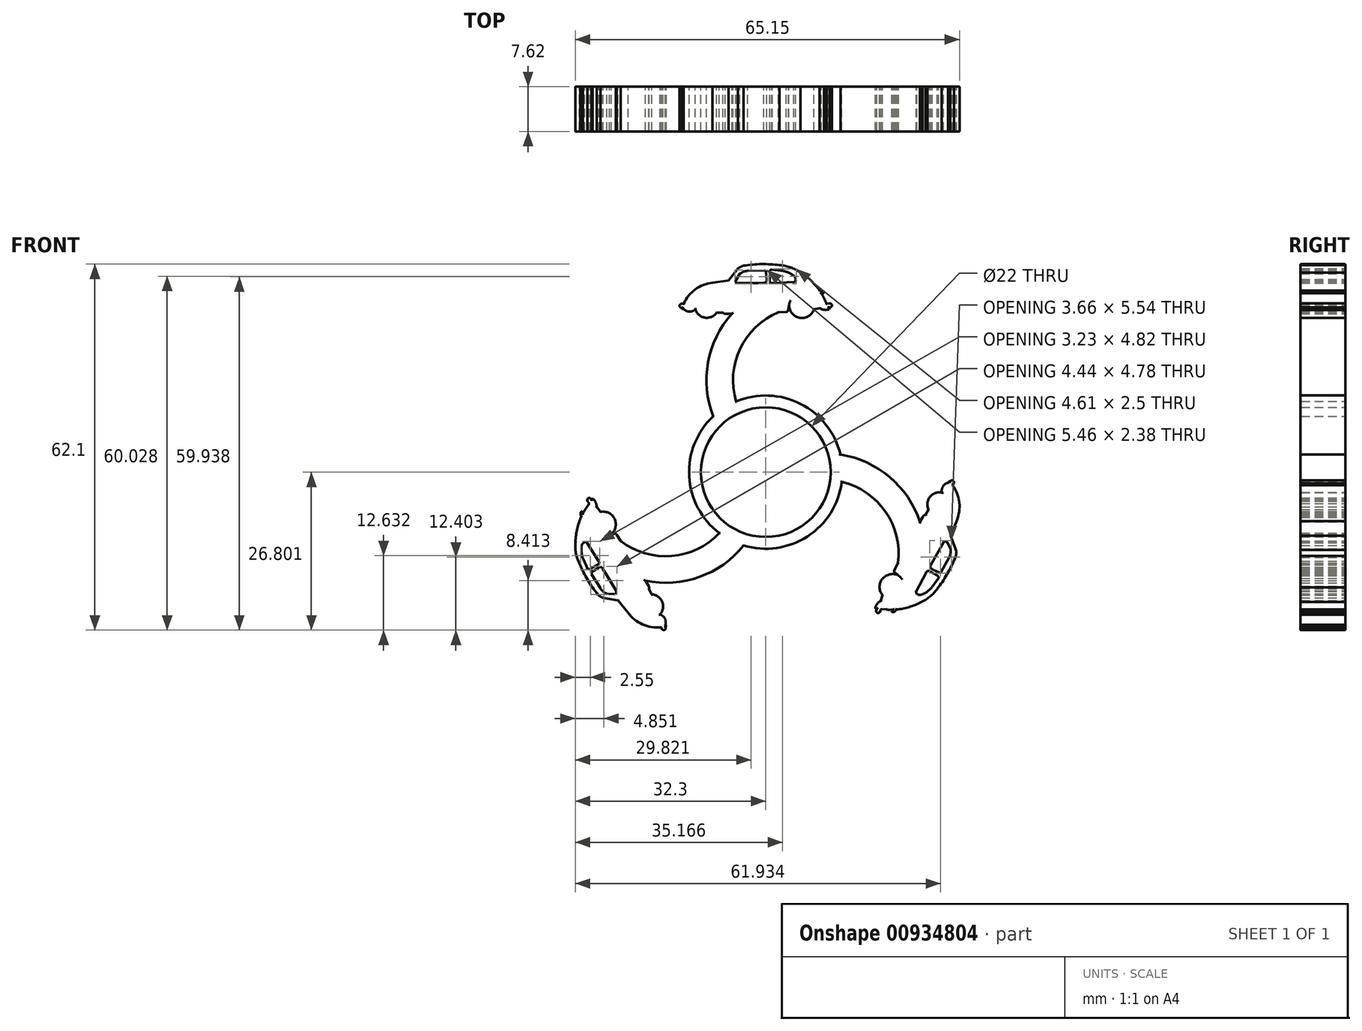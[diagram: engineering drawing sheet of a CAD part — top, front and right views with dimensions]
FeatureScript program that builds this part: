
annotation { "Feature Type Name" : "Feature", "Feature Type Description" : "" }
export const myFeature = defineFeature(function(context is Context, id is Id, definition is map)
    precondition{}
    {
        {
            var Q0;
            Q0=qCreatedBy(makeId("Front.planeOp"),FACE);
            var sketch = newSketch(context, id + "F0", { "sketchPlane" : qUnion([Q0])});
            skArc(sketch, "E0", {"start": v(-9, 14.46) * mm, "mid": v(-11.94, 13.3) * mm, "end": v(-13.92, 10.85) * mm});
            skArc(sketch, "E1", {"start": v(5.88, 16.16) * mm, "mid": v(4.19, 17.04) * mm, "end": v(2.31, 17.41) * mm});
            skArc(sketch, "E2", {"start": v(-11.95, 9.91) * mm, "mid": v(-10.3, 8.52) * mm, "end": v(-8.3, 9.38) * mm});
            skArc(sketch, "E3", {"start": v(3.95, 10.62) * mm, "mid": v(5.76, 8.48) * mm, "end": v(8.18, 9.91) * mm});
            skPoint(sketch, "E4.first.point", {"position": v(-7.38, 9.64) * mm});
            skPoint(sketch, "E4.second.point", {"position": v(-12.35, 9.96) * mm});
            skPoint(sketch, "E4.third.point", {"position": v(-12.18, 8.98) * mm});
            skPoint(sketch, "E5.first.point", {"position": v(4.32, 11.24) * mm});
            skPoint(sketch, "E5.second.point", {"position": v(8.47, 9.2) * mm});
            skPoint(sketch, "E5.third.point", {"position": v(6.12, 12.43) * mm});
            skLineSegment(sketch, "E6", {"start": v(-6.33, 14.84) * mm, "end": v(-4.7, 16.85) * mm});
            skLineSegment(sketch, "E7", {"start": v(-6.33, 14.84) * mm, "end": v(-9, 14.46) * mm});
            skPoint(sketch, "E8.second.point", {"position": v(-1.28, 12.75) * mm});
            skPoint(sketch, "E8.third.point", {"position": v(-0.45, 14.03) * mm});
            skPoint(sketch, "E9.first.point", {"position": v(8.75, 10.46) * mm});
            skPoint(sketch, "E9.second.point", {"position": v(10.03, 11.1) * mm});
            skPoint(sketch, "E9.third.point", {"position": v(9.87, 11.34) * mm});
            skPoint(sketch, "E10.first.point", {"position": v(8.43, 11.1) * mm});
            skPoint(sketch, "E10.second.point", {"position": v(11.08, 13.13) * mm});
            skPoint(sketch, "E10.third.point", {"position": v(10.99, 13.19) * mm});
            skPoint(sketch, "E11.first.point", {"position": v(7.66, 14.8) * mm});
            skPoint(sketch, "E11.second.point", {"position": v(-6.04, -1.6) * mm});
            skPoint(sketch, "E11.third.point", {"position": v(8.43, 0) * mm});
            skArc(sketch, "E12", {"start": v(-14.24, 10) * mm, "mid": v(-14.07, 9.98) * mm, "end": v(-13.9, 9.97) * mm});
            skPoint(sketch, "E12.first.point", {"position": v(-12.18, 10.81) * mm});
            skPoint(sketch, "E12.second.point", {"position": v(-15.7, 13.16) * mm});
            skPoint(sketch, "E12.third.point", {"position": v(-15.23, 10.47) * mm});
            skArc(sketch, "E13", {"start": v(-7.27, 9.38) * mm, "mid": v(-6.98, 9.18) * mm, "end": v(-6.64, 9.16) * mm});
            skPoint(sketch, "E13.second.point", {"position": v(-6.18, 9.92) * mm});
            skPoint(sketch, "E13.third.point", {"position": v(-6.88, 9.15) * mm});
            skLineSegment(sketch, "E14.trimOffspring", {"start": v(-6.88, 9.15) * mm, "end": v(-6.64, 9.16) * mm});
            skArc(sketch, "E15.trimOffspring", {"start": v(-3.79, 17.33) * mm, "mid": v(-4.26, 17.13) * mm, "end": v(-4.7, 16.85) * mm});
            skArc(sketch, "E16.trimOffspring", {"start": v(11.08, 13.13) * mm, "mid": v(11.04, 13.16) * mm, "end": v(10.99, 13.19) * mm});
            skArc(sketch, "E17.trimOffspring", {"start": v(9.96, 11.68) * mm, "mid": v(9.71, 12.17) * mm, "end": v(9.43, 12.65) * mm});
            skPoint(sketch, "E18.first.point", {"position": v(-7.48, 10.06) * mm});
            skPoint(sketch, "E18.second.point", {"position": v(-12.85, 9.43) * mm});
            skPoint(sketch, "E18.third.point", {"position": v(-11.36, 7.32) * mm});
            skArc(sketch, "E19", {"start": v(2.31, 17.41) * mm, "mid": v(-0.74, 17.6) * mm, "end": v(-3.79, 17.33) * mm});
            skPoint(sketch, "E19.second.point", {"position": v(2.31, -24.55) * mm});
            skPoint(sketch, "E20.end.orphan", {"position": v(2.31, 17.41) * mm});
            skArc(sketch, "E21", {"start": v(9.86, 12.65) * mm, "mid": v(9.6, 13.04) * mm, "end": v(9.13, 13.1) * mm});
            skPoint(sketch, "E21.first.point", {"position": v(9.13, 13.1) * mm});
            skPoint(sketch, "E21.second.point", {"position": v(9.36, 12) * mm});
            skPoint(sketch, "E21.third.point", {"position": v(9.7, 12.18) * mm});
            skLineSegment(sketch, "E22", {"start": v(9.86, 12.65) * mm, "end": v(9.43, 12.65) * mm});
            skArc(sketch, "E23.trimOffspring", {"start": v(9.13, 13.1) * mm, "mid": v(7.67, 14.8) * mm, "end": v(5.88, 16.16) * mm});
            skLineSegment(sketch, "E24", {"start": v(9.96, 11.68) * mm, "end": v(10.35, 10.9) * mm});
            skArc(sketch, "E25", {"start": v(10.9, 10.25) * mm, "mid": v(11.21, 10.61) * mm, "end": v(10.85, 10.93) * mm});
            skLineSegment(sketch, "E26", {"start": v(10.9, 10.25) * mm, "end": v(10.67, 10.23) * mm});
            skLineSegment(sketch, "E27", {"start": v(10.85, 10.93) * mm, "end": v(10.35, 10.9) * mm});
            skPoint(sketch, "E27.endSnap0", {"position": v(10.38, 10.82) * mm});
            skPoint(sketch, "E28.orphan", {"position": v(10.38, 10.9) * mm});
            skArc(sketch, "E29", {"start": v(-14.25, 10.85) * mm, "mid": v(-14.6, 10.54) * mm, "end": v(-14.3, 10.18) * mm});
            skArc(sketch, "E30.trimOffspring", {"start": v(-14.18, 10.18) * mm, "mid": v(-14.2, 10.1) * mm, "end": v(-14.24, 10) * mm});
            skLineSegment(sketch, "E31", {"start": v(-14.29, 10.85) * mm, "end": v(-13.92, 10.85) * mm});
            skLineSegment(sketch, "E32", {"start": v(-14.3, 10.18) * mm, "end": v(-14.18, 10.18) * mm});
            skPoint(sketch, "E33.orphan", {"position": v(-13.91, 10.19) * mm});
            skPoint(sketch, "E34.orphan", {"position": v(-14.18, 10.19) * mm});
            skLineSegment(sketch, "E35.trimOffspring", {"start": v(10.67, 10.23) * mm, "end": v(10.8, 9.96) * mm});
            skPoint(sketch, "E36.first.point", {"position": v(4.65, 11.8) * mm});
            skPoint(sketch, "E36.second.point", {"position": v(7.99, 8.17) * mm});
            skPoint(sketch, "E36.third.point", {"position": v(8.67, 9.2) * mm});
            skArc(sketch, "E37", {"start": v(3.48, 9.5) * mm, "mid": v(3.69, 9.57) * mm, "end": v(3.8, 9.77) * mm});
            skPoint(sketch, "E37.first.point", {"position": v(3.8, 9.85) * mm});
            skPoint(sketch, "E37.second.point", {"position": v(3.15, 9.78) * mm});
            skPoint(sketch, "E37.third.point", {"position": v(3.48, 9.5) * mm});
            skLineSegment(sketch, "E38", {"start": v(3.88, 10.28) * mm, "end": v(3.8, 9.77) * mm});
            skArc(sketch, "E39.trimOffspring", {"start": v(3.95, 10.62) * mm, "mid": v(3.9, 10.45) * mm, "end": v(3.88, 10.28) * mm});
            skPoint(sketch, "E40.first.point", {"position": v(-0.4, 16.47) * mm});
            skPoint(sketch, "E40.second.point", {"position": v(-0.1, 15.95) * mm});
            skPoint(sketch, "E40.third.point", {"position": v(-0.25, 15.93) * mm});
            skArc(sketch, "E41", {"start": v(-0.35, 14.4) * mm, "mid": v(0.04, 14.58) * mm, "end": v(0.14, 15) * mm});
            skPoint(sketch, "E41.first.point", {"position": v(0.14, 14.78) * mm});
            skPoint(sketch, "E41.second.point", {"position": v(-0.81, 15.05) * mm});
            skPoint(sketch, "E41.third.point", {"position": v(-0.35, 14.4) * mm});
            skArc(sketch, "E42", {"start": v(-5.03, 14.94) * mm, "mid": v(-5.07, 14.55) * mm, "end": v(-4.73, 14.35) * mm});
            skPoint(sketch, "E42.first.point", {"position": v(-4.93, 14.4) * mm});
            skPoint(sketch, "E42.second.point", {"position": v(-4.52, 15) * mm});
            skPoint(sketch, "E42.third.point", {"position": v(-4.7, 15.07) * mm});
            skArc(sketch, "E43", {"start": v(-3.04, 16.45) * mm, "mid": v(-3.75, 16.32) * mm, "end": v(-4.37, 15.95) * mm});
            skPoint(sketch, "E43.first.point", {"position": v(-4.37, 15.95) * mm});
            skPoint(sketch, "E43.second.point", {"position": v(-1.65, 12.8) * mm});
            skPoint(sketch, "E43.third.point", {"position": v(-0.98, 14.72) * mm});
            skLineSegment(sketch, "E44", {"start": v(-4.37, 15.95) * mm, "end": v(-5.05, 14.9) * mm});
            skLineSegment(sketch, "E45", {"start": v(-3.04, 16.45) * mm, "end": v(-0.23, 16.53) * mm});
            skLineSegment(sketch, "E46", {"start": v(-4.73, 14.35) * mm, "end": v(-0.35, 14.4) * mm});
            skLineSegment(sketch, "E47", {"start": v(0.14, 15) * mm, "end": v(0.07, 16.24) * mm});
            skArc(sketch, "E48.trimOffspring", {"start": v(0.07, 16.24) * mm, "mid": v(-0.1, 16.5) * mm, "end": v(-0.4, 16.47) * mm});
            skArc(sketch, "E49.trimOffspring", {"start": v(-5.03, 14.95) * mm, "mid": v(-5.03, 14.95) * mm, "end": v(-5.03, 14.94) * mm});
            skArc(sketch, "E50", {"start": v(1, 16.68) * mm, "mid": v(0.74, 16.54) * mm, "end": v(0.66, 16.26) * mm});
            skPoint(sketch, "E50.first.point", {"position": v(0.66, 16.33) * mm});
            skPoint(sketch, "E50.second.point", {"position": v(1.43, 16.2) * mm});
            skPoint(sketch, "E50.third.point", {"position": v(0.85, 15.96) * mm});
            skArc(sketch, "E51", {"start": v(0.67, 14.75) * mm, "mid": v(0.79, 14.45) * mm, "end": v(1.11, 14.4) * mm});
            skPoint(sketch, "E51.first.point", {"position": v(0.67, 14.75) * mm});
            skPoint(sketch, "E51.second.point", {"position": v(1.33, 14.68) * mm});
            skPoint(sketch, "E51.third.point", {"position": v(1.32, 14.78) * mm});
            skPoint(sketch, "E52.first.point", {"position": v(5, 14.62) * mm});
            skPoint(sketch, "E52.second.point", {"position": v(3.45, 15.3) * mm});
            skPoint(sketch, "E52.third.point", {"position": v(3.55, 14.43) * mm});
            skArc(sketch, "E53", {"start": v(0.66, 16.29) * mm, "mid": v(0.66, 16.29) * mm, "end": v(0.66, 16.29) * mm});
            skPoint(sketch, "E53.first.point", {"position": v(4.74, 15.63) * mm});
            skPoint(sketch, "E53.second.point", {"position": v(-0.68, 8.76) * mm});
            skPoint(sketch, "E53.third.point", {"position": v(1.58, 16.5) * mm});
            skArc(sketch, "E54", {"start": v(4.77, 14.54) * mm, "mid": v(4.95, 14.63) * mm, "end": v(5.06, 14.8) * mm});
            skPoint(sketch, "E54.first.point", {"position": v(4.77, 14.54) * mm});
            skPoint(sketch, "E54.second.point", {"position": v(4.56, 15.33) * mm});
            skPoint(sketch, "E54.third.point", {"position": v(4.52, 15.32) * mm});
            skLineSegment(sketch, "E55", {"start": v(1.11, 14.4) * mm, "end": v(4.77, 14.54) * mm});
            skLineSegment(sketch, "E56", {"start": v(1, 16.68) * mm, "end": v(2.59, 16.5) * mm});
            skLineSegment(sketch, "E57", {"start": v(0.66, 16.33) * mm, "end": v(0.67, 14.75) * mm});
            skArc(sketch, "E58.trimOffspring", {"start": v(5.06, 14.8) * mm, "mid": v(5.02, 15.26) * mm, "end": v(4.74, 15.63) * mm});
            skArc(sketch, "E59.trimOffspring", {"start": v(4.74, 15.63) * mm, "mid": v(3.72, 16.2) * mm, "end": v(2.59, 16.5) * mm});
            skPoint(sketch, "E60.first.point", {"position": v(-13.14, 9.56) * mm});
            skPoint(sketch, "E60.second.point", {"position": v(-12.49, 12.22) * mm});
            skPoint(sketch, "E60.third.point", {"position": v(-12.69, 12.26) * mm});
            skArc(sketch, "E61.trimOffspring", {"start": v(-13.9, 9.97) * mm, "mid": v(-12.93, 9.54) * mm, "end": v(-11.95, 9.91) * mm});
            skLineSegment(sketch, "E62", {"start": v(-8.3, 9.38) * mm, "end": v(-7.27, 9.38) * mm});
            skLineSegment(sketch, "E63", {"start": v(8.18, 9.91) * mm, "end": v(9.21, 10.1) * mm});
            skArc(sketch, "E64.trimOffspring", {"start": v(9.21, 10.1) * mm, "mid": v(10, 9.84) * mm, "end": v(10.8, 9.96) * mm});
            skPoint(sketch, "E65.1.0", {"position": v(-30.88, -30.27) * mm});
            skPoint(sketch, "E65.1.1", {"position": v(-19.6, -43.67) * mm});
            skPoint(sketch, "E65.1.2", {"position": v(-16.78, -44.97) * mm});
            skPoint(sketch, "E65.1.3", {"position": v(-31.57, -33.25) * mm});
            skPoint(sketch, "E65.1.4", {"position": v(-27.95, -34.77) * mm});
            skPoint(sketch, "E65.1.5", {"position": v(-30.08, -23.67) * mm});
            skPoint(sketch, "E65.1.6", {"position": v(-32.24, -23.63) * mm});
            skPoint(sketch, "E65.1.7", {"position": v(-31.98, -27.31) * mm});
            skPoint(sketch, "E65.1.8", {"position": v(-29.8, -34.14) * mm});
            skPoint(sketch, "E65.1.9", {"position": v(-17.04, -42.7) * mm});
            skPoint(sketch, "E65.1.10", {"position": v(-25.76, -28.18) * mm});
            skPoint(sketch, "E65.1.11", {"position": v(-10.93, -30.98) * mm});
            skPoint(sketch, "E65.1.12", {"position": v(4.78, -12.27) * mm});
            skPoint(sketch, "E65.1.13", {"position": v(-29.6, -30.69) * mm});
            skPoint(sketch, "E65.1.14", {"position": v(-22.57, -31.51) * mm});
            skPoint(sketch, "E65.1.15", {"position": v(-32.24, -23.51) * mm});
            skPoint(sketch, "E65.1.16", {"position": v(-19.99, -37.76) * mm});
            skPoint(sketch, "E65.1.17", {"position": v(-29.57, -33.8) * mm});
            skPoint(sketch, "E65.1.18", {"position": v(-29.4, -35.13) * mm});
            skPoint(sketch, "E65.1.19", {"position": v(-17.06, -43.92) * mm});
            skPoint(sketch, "E65.1.20", {"position": v(-19.81, -37.08) * mm});
            skPoint(sketch, "E65.1.21", {"position": v(-17.01, -41.58) * mm});
            skPoint(sketch, "E65.1.22", {"position": v(-30.3, -31.21) * mm});
            skPoint(sketch, "E65.1.23", {"position": v(-25.28, -28.28) * mm});
            skPoint(sketch, "E65.1.24", {"position": v(-26.96, -38.31) * mm});
            skPoint(sketch, "E65.1.25", {"position": v(-26.03, -38.15) * mm});
            skPoint(sketch, "E65.1.26", {"position": v(-25.73, -34.03) * mm});
            skPoint(sketch, "E65.1.27", {"position": v(-27.63, -23.64) * mm});
            skPoint(sketch, "E65.1.28", {"position": v(-20.3, -38.05) * mm});
            skPoint(sketch, "E65.1.29", {"position": v(-17.07, -42.39) * mm});
            skPoint(sketch, "E65.1.30", {"position": v(-27.25, -33.95) * mm});
            skPoint(sketch, "E65.1.31", {"position": v(-17.78, -42.23) * mm});
            skPoint(sketch, "E65.1.32", {"position": v(-19.54, -19.25) * mm});
            skPoint(sketch, "E65.1.33", {"position": v(-15.99, -40.05) * mm});
            skPoint(sketch, "E65.1.34", {"position": v(-20.83, -36.87) * mm});
            skPoint(sketch, "E65.1.35", {"position": v(-28.2, -33.82) * mm});
            skPoint(sketch, "E65.1.36", {"position": v(-18.87, -46.72) * mm});
            skPoint(sketch, "E65.1.37", {"position": v(-26.4, -23.72) * mm});
            skPoint(sketch, "E65.1.38", {"position": v(-30.5, -29.52) * mm});
            skPoint(sketch, "E65.1.39", {"position": v(-29.15, -27.46) * mm});
            skLineSegment(sketch, "E65.1.40", {"start": v(-19.81, -37.08) * mm, "end": v(-20.4, -36.13) * mm});
            skPoint(sketch, "E65.1.41", {"position": v(-31.24, -25.19) * mm});
            skPoint(sketch, "E65.1.42", {"position": v(-29.96, -23.41) * mm});
            skArc(sketch, "E65.1.43", {"start": v(-17.94, -41.85) * mm, "mid": v(-17.56, -39.72) * mm, "end": v(-19.3, -38.43) * mm});
            skPoint(sketch, "E65.1.44", {"position": v(-27.53, -23.81) * mm});
            skPoint(sketch, "E65.1.45", {"position": v(-29.9, -22.97) * mm});
            skPoint(sketch, "E65.1.46", {"position": v(-30.72, -24.23) * mm});
            skPoint(sketch, "E65.1.47", {"position": v(-18.6, -42.5) * mm});
            skPoint(sketch, "E65.1.48", {"position": v(-30.86, -30.29) * mm});
            skPoint(sketch, "E65.1.49", {"position": v(-26.05, -37.96) * mm});
            skPoint(sketch, "E65.1.50", {"position": v(-27.62, -34.05) * mm});
            skPoint(sketch, "E65.1.51", {"position": v(-19.67, -43.47) * mm});
            skPoint(sketch, "E65.1.52", {"position": v(-17.2, -43.69) * mm});
            skPoint(sketch, "E65.1.53", {"position": v(-29, -34.73) * mm});
            skPoint(sketch, "E65.1.54", {"position": v(-27.88, -28.42) * mm});
            skPoint(sketch, "E65.1.55", {"position": v(-30.4, -33.42) * mm});
            skPoint(sketch, "E65.1.56", {"position": v(-25.6, -34.38) * mm});
            skPoint(sketch, "E65.1.57", {"position": v(-27.22, -28.43) * mm});
            skPoint(sketch, "E65.1.58", {"position": v(-28.76, -24.2) * mm});
            skPoint(sketch, "E65.1.59", {"position": v(-25.37, -28.7) * mm});
            skPoint(sketch, "E65.1.60", {"position": v(-28.79, -32.8) * mm});
            skPoint(sketch, "E65.1.61", {"position": v(-25.33, -38.02) * mm});
            skPoint(sketch, "E65.1.62", {"position": v(-30.3, -29.68) * mm});
            skPoint(sketch, "E65.1.63", {"position": v(-27.59, -34.76) * mm});
            skPoint(sketch, "E65.1.64", {"position": v(-29.15, -24.8) * mm});
            skArc(sketch, "E65.1.65", {"start": v(-23.35, -41.58) * mm, "mid": v(-20.88, -43.53) * mm, "end": v(-17.77, -44.03) * mm});
            skPoint(sketch, "E65.1.66", {"position": v(-29.1, -34.62) * mm});
            skArc(sketch, "E65.1.67", {"start": v(-26.5, -28.44) * mm, "mid": v(-25.56, -25.8) * mm, "end": v(-28, -24.42) * mm});
            skPoint(sketch, "E65.1.68", {"position": v(-30.4, -24.44) * mm});
            skPoint(sketch, "E65.1.69", {"position": v(-28.7, -32.74) * mm});
            skArc(sketch, "E65.1.70", {"start": v(-31.24, -25.19) * mm, "mid": v(-31.98, -27.3) * mm, "end": v(-32.26, -29.53) * mm});
            skPoint(sketch, "E65.1.71", {"position": v(-28.44, -33.35) * mm});
            skPoint(sketch, "E65.1.72", {"position": v(-31.23, -30.26) * mm});
            skPoint(sketch, "E65.1.73", {"position": v(-30.08, -33.41) * mm});
            skPoint(sketch, "E65.1.74", {"position": v(-29.96, -23) * mm});
            skLineSegment(sketch, "E65.1.75", {"start": v(-25.01, -39.45) * mm, "end": v(-23.35, -41.58) * mm});
            skArc(sketch, "E65.1.76", {"start": v(-19.82, -37.53) * mm, "mid": v(-19.78, -37.18) * mm, "end": v(-19.94, -36.87) * mm});
            skLineSegment(sketch, "E65.1.77", {"start": v(-19.3, -38.43) * mm, "end": v(-19.82, -37.53) * mm});
            skArc(sketch, "E65.1.78", {"start": v(-28.44, -38.5) * mm, "mid": v(-28.03, -38.8) * mm, "end": v(-27.57, -39.04) * mm});
            skArc(sketch, "E65.1.79", {"start": v(-32.26, -29.53) * mm, "mid": v(-32.18, -31.44) * mm, "end": v(-31.57, -33.25) * mm});
            skArc(sketch, "E65.1.80", {"start": v(-31.57, -33.25) * mm, "mid": v(-30.2, -35.99) * mm, "end": v(-28.44, -38.5) * mm});
            skLineSegment(sketch, "E65.1.81", {"start": v(-25.01, -39.45) * mm, "end": v(-27.57, -39.04) * mm});
            skArc(sketch, "E65.1.82", {"start": v(-17.02, -43.57) * mm, "mid": v(-17.12, -42.52) * mm, "end": v(-17.94, -41.85) * mm});
            skLineSegment(sketch, "E65.1.84", {"start": v(-28.05, -37.4) * mm, "end": v(-29.52, -35.01) * mm});
            skLineSegment(sketch, "E65.1.85", {"start": v(-26.17, -28.32) * mm, "end": v(-25.69, -28.14) * mm});
            skArc(sketch, "E65.1.86", {"start": v(-28.05, -37.4) * mm, "mid": v(-27.58, -37.95) * mm, "end": v(-26.96, -38.31) * mm});
            skLineSegment(sketch, "E65.1.87", {"start": v(-28.35, -32.78) * mm, "end": v(-30.3, -29.68) * mm});
            skArc(sketch, "E65.1.88", {"start": v(-31.23, -30.26) * mm, "mid": v(-31.22, -31.43) * mm, "end": v(-30.9, -32.56) * mm});
            skLineSegment(sketch, "E65.1.89", {"start": v(-25.39, -37.82) * mm, "end": v(-27.62, -34.05) * mm});
            skArc(sketch, "E65.1.90", {"start": v(-26.5, -28.44) * mm, "mid": v(-26.33, -28.39) * mm, "end": v(-26.17, -28.32) * mm});
            skArc(sketch, "E65.1.91", {"start": v(-30.3, -29.68) * mm, "mid": v(-30.47, -29.58) * mm, "end": v(-30.68, -29.57) * mm});
            skArc(sketch, "E65.1.92", {"start": v(-25.28, -28.28) * mm, "mid": v(-25.46, -28.14) * mm, "end": v(-25.69, -28.14) * mm});
            skArc(sketch, "E65.1.93", {"start": v(-30.68, -29.57) * mm, "mid": v(-31.05, -29.83) * mm, "end": v(-31.23, -30.26) * mm});
            skLineSegment(sketch, "E65.1.94", {"start": v(-28, -24.42) * mm, "end": v(-28.67, -23.62) * mm});
            skArc(sketch, "E65.1.95", {"start": v(-31.2, -24.33) * mm, "mid": v(-31.42, -24.75) * mm, "end": v(-31.24, -25.19) * mm});
            skLineSegment(sketch, "E65.1.96", {"start": v(-30.27, -34.03) * mm, "end": v(-30.9, -32.56) * mm});
            skArc(sketch, "E65.1.97", {"start": v(-30.42, -23.76) * mm, "mid": v(-30.72, -24.22) * mm, "end": v(-31, -24.7) * mm});
            skArc(sketch, "E65.1.98", {"start": v(-32.24, -23.51) * mm, "mid": v(-32.24, -23.57) * mm, "end": v(-32.24, -23.63) * mm});
            skArc(sketch, "E65.1.99", {"start": v(-28.44, -33.35) * mm, "mid": v(-28.23, -33.1) * mm, "end": v(-28.35, -32.78) * mm});
            skArc(sketch, "E65.1.100", {"start": v(-29.43, -34.6) * mm, "mid": v(-29.57, -34.88) * mm, "end": v(-29.4, -35.13) * mm});
            skLineSegment(sketch, "E65.1.101", {"start": v(-28.4, -33.93) * mm, "end": v(-29.43, -34.6) * mm});
            skArc(sketch, "E65.1.102", {"start": v(-27.62, -34.05) * mm, "mid": v(-27.98, -33.8) * mm, "end": v(-28.4, -33.93) * mm});
            skArc(sketch, "E65.1.103", {"start": v(-30.27, -34.03) * mm, "mid": v(-30.02, -34.17) * mm, "end": v(-29.74, -34.1) * mm});
            skArc(sketch, "E65.1.104", {"start": v(-29.76, -34.12) * mm, "mid": v(-29.76, -34.12) * mm, "end": v(-29.76, -34.12) * mm});
            skLineSegment(sketch, "E65.1.105", {"start": v(-29.8, -34.14) * mm, "end": v(-28.44, -33.35) * mm});
            skLineSegment(sketch, "E65.1.106", {"start": v(-31.2, -24.33) * mm, "end": v(-31, -24.7) * mm});
            skArc(sketch, "E65.1.107", {"start": v(-17.6, -44.31) * mm, "mid": v(-17.15, -44.47) * mm, "end": v(-17, -44.02) * mm});
            skLineSegment(sketch, "E65.1.108", {"start": v(-26.96, -38.31) * mm, "end": v(-25.71, -38.38) * mm});
            skArc(sketch, "E65.1.109", {"start": v(-25.75, -38.37) * mm, "mid": v(-25.4, -38.22) * mm, "end": v(-25.39, -37.82) * mm});
            skLineSegment(sketch, "E65.1.110", {"start": v(-17.58, -44.35) * mm, "end": v(-17.77, -44.03) * mm});
            skArc(sketch, "E65.1.111", {"start": v(-16.87, -43.88) * mm, "mid": v(-16.94, -43.72) * mm, "end": v(-17.02, -43.57) * mm});
            skLineSegment(sketch, "E65.1.112", {"start": v(-17, -44.02) * mm, "end": v(-17.05, -43.92) * mm});
            skArc(sketch, "E65.1.113", {"start": v(-17.05, -43.92) * mm, "mid": v(-16.96, -43.9) * mm, "end": v(-16.87, -43.88) * mm});
            skLineSegment(sketch, "E65.1.114", {"start": v(-29.53, -22.42) * mm, "end": v(-29.36, -22.17) * mm});
            skArc(sketch, "E65.1.115", {"start": v(-25.76, -38.38) * mm, "mid": v(-25.76, -38.37) * mm, "end": v(-25.75, -38.37) * mm});
            skArc(sketch, "E65.1.116", {"start": v(-29.65, -22.23) * mm, "mid": v(-30.13, -22.14) * mm, "end": v(-30.21, -22.62) * mm});
            skLineSegment(sketch, "E65.1.117", {"start": v(-30.42, -23.76) * mm, "end": v(-29.94, -23.03) * mm});
            skArc(sketch, "E65.1.118", {"start": v(-28.67, -23.62) * mm, "mid": v(-28.85, -22.82) * mm, "end": v(-29.36, -22.17) * mm});
            skLineSegment(sketch, "E65.1.119", {"start": v(-30.21, -22.62) * mm, "end": v(-29.94, -23.03) * mm});
            skLineSegment(sketch, "E65.1.120", {"start": v(-29.65, -22.23) * mm, "end": v(-29.53, -22.42) * mm});
            skPoint(sketch, "E65.2.0", {"position": v(26.33, -38.16) * mm});
            skPoint(sketch, "E65.2.1", {"position": v(32.3, -21.7) * mm});
            skPoint(sketch, "E65.2.2", {"position": v(32, -18.6) * mm});
            skPoint(sketch, "E65.2.3", {"position": v(29.25, -37.26) * mm});
            skPoint(sketch, "E65.2.4", {"position": v(28.77, -33.37) * mm});
            skPoint(sketch, "E65.2.5", {"position": v(20.21, -40.76) * mm});
            skPoint(sketch, "E65.2.6", {"position": v(21.26, -42.66) * mm});
            skPoint(sketch, "E65.2.7", {"position": v(24.32, -40.59) * mm});
            skPoint(sketch, "E65.2.8", {"position": v(29.14, -35.28) * mm});
            skPoint(sketch, "E65.2.9", {"position": v(30.18, -19.95) * mm});
            skPoint(sketch, "E65.2.10", {"position": v(21.96, -34.77) * mm});
            skPoint(sketch, "E65.2.11", {"position": v(16.96, -20.52) * mm});
            skPoint(sketch, "E65.2.12", {"position": v(-7.1, -16.28) * mm});
            skPoint(sketch, "E65.2.13", {"position": v(26.05, -36.84) * mm});
            skPoint(sketch, "E65.2.14", {"position": v(23.25, -30.34) * mm});
            skPoint(sketch, "E65.2.15", {"position": v(21.16, -42.71) * mm});
            skPoint(sketch, "E65.2.16", {"position": v(27.37, -24.98) * mm});
            skPoint(sketch, "E65.2.17", {"position": v(28.72, -35.26) * mm});
            skPoint(sketch, "E65.2.18", {"position": v(29.79, -34.44) * mm});
            skPoint(sketch, "E65.2.19", {"position": v(31.24, -19.36) * mm});
            skPoint(sketch, "E65.2.20", {"position": v(26.7, -25.16) * mm});
            skPoint(sketch, "E65.2.21", {"position": v(29.19, -20.5) * mm});
            skPoint(sketch, "E65.2.22", {"position": v(26.85, -37.18) * mm});
            skPoint(sketch, "E65.2.23", {"position": v(21.8, -34.3) * mm});
            skPoint(sketch, "E65.2.24", {"position": v(31.33, -30.74) * mm});
            skPoint(sketch, "E65.2.25", {"position": v(30.73, -30.02) * mm});
            skPoint(sketch, "E65.2.26", {"position": v(27.01, -31.82) * mm});
            skPoint(sketch, "E65.2.27", {"position": v(18.96, -38.66) * mm});
            skPoint(sketch, "E65.2.28", {"position": v(27.78, -25.1) * mm});
            skPoint(sketch, "E65.2.29", {"position": v(29.92, -20.14) * mm});
            skPoint(sketch, "E65.2.30", {"position": v(27.7, -33.17) * mm});
            skPoint(sketch, "E65.2.31", {"position": v(30.13, -20.83) * mm});
            skPoint(sketch, "E65.2.32", {"position": v(11.11, -33.85) * mm});
            skPoint(sketch, "E65.2.33", {"position": v(27.35, -20.37) * mm});
            skPoint(sketch, "E65.2.34", {"position": v(27.01, -26.15) * mm});
            skPoint(sketch, "E65.2.35", {"position": v(28.06, -34.06) * mm});
            skPoint(sketch, "E65.2.36", {"position": v(34.57, -19.53) * mm});
            skPoint(sketch, "E65.2.37", {"position": v(18.41, -37.55) * mm});
            skPoint(sketch, "E65.2.38", {"position": v(25.49, -38.2) * mm});
            skPoint(sketch, "E65.2.39", {"position": v(23.03, -38.07) * mm});
            skLineSegment(sketch, "E65.2.40", {"start": v(26.58, -25.38) * mm, "end": v(26.16, -26.16) * mm});
            skPoint(sketch, "E65.2.41", {"position": v(22.1, -41) * mm});
            skPoint(sketch, "E65.2.42", {"position": v(19.93, -40.79) * mm});
            skArc(sketch, "E65.2.43", {"start": v(29.89, -21.16) * mm, "mid": v(27.85, -21.9) * mm, "end": v(27.6, -24.04) * mm});
            skPoint(sketch, "E65.2.44", {"position": v(19.06, -38.49) * mm});
            skPoint(sketch, "E65.2.45", {"position": v(19.5, -40.95) * mm});
            skPoint(sketch, "E65.2.46", {"position": v(21.02, -41.04) * mm});
            skPoint(sketch, "E65.2.47", {"position": v(30.78, -21.4) * mm});
            skPoint(sketch, "E65.2.48", {"position": v(26.33, -38.13) * mm});
            skPoint(sketch, "E65.2.49", {"position": v(30.57, -30.13) * mm});
            skPoint(sketch, "E65.2.50", {"position": v(27.97, -33.44) * mm});
            skPoint(sketch, "E65.2.51", {"position": v(32.15, -21.84) * mm});
            skPoint(sketch, "E65.2.52", {"position": v(31.1, -19.6) * mm});
            skPoint(sketch, "E65.2.53", {"position": v(29.25, -34.3) * mm});
            skPoint(sketch, "E65.2.54", {"position": v(23.22, -36.48) * mm});
            skPoint(sketch, "E65.2.55", {"position": v(28.82, -36.17) * mm});
            skPoint(sketch, "E65.2.56", {"position": v(27.25, -31.52) * mm});
            skPoint(sketch, "E65.2.57", {"position": v(22.9, -35.91) * mm});
            skPoint(sketch, "E65.2.58", {"position": v(20, -39.36) * mm});
            skPoint(sketch, "E65.2.59", {"position": v(22.22, -34.16) * mm});
            skPoint(sketch, "E65.2.60", {"position": v(27.47, -35.08) * mm});
            skPoint(sketch, "E65.2.61", {"position": v(30.26, -29.48) * mm});
            skPoint(sketch, "E65.2.62", {"position": v(25.53, -37.95) * mm});
            skPoint(sketch, "E65.2.63", {"position": v(28.57, -33.06) * mm});
            skPoint(sketch, "E65.2.64", {"position": v(20.72, -39.4) * mm});
            skArc(sketch, "E65.2.65", {"start": v(32.35, -25.98) * mm, "mid": v(32.81, -22.86) * mm, "end": v(31.69, -19.92) * mm});
            skPoint(sketch, "E65.2.66", {"position": v(29.2, -34.43) * mm});
            skArc(sketch, "E65.2.67", {"start": v(22.55, -35.27) * mm, "mid": v(19.8, -35.78) * mm, "end": v(19.82, -38.59) * mm});
            skPoint(sketch, "E65.2.68", {"position": v(21.04, -40.66) * mm});
            skPoint(sketch, "E65.2.69", {"position": v(27.38, -35.04) * mm});
            skArc(sketch, "E65.2.70", {"start": v(22.1, -41) * mm, "mid": v(24.3, -40.59) * mm, "end": v(26.38, -39.72) * mm});
            skPoint(sketch, "E65.2.71", {"position": v(27.77, -34.5) * mm});
            skPoint(sketch, "E65.2.72", {"position": v(26.5, -38.47) * mm});
            skPoint(sketch, "E65.2.73", {"position": v(28.65, -35.9) * mm});
            skPoint(sketch, "E65.2.74", {"position": v(19.57, -40.99) * mm});
            skLineSegment(sketch, "E65.2.75", {"start": v(31.34, -28.48) * mm, "end": v(32.35, -25.98) * mm});
            skArc(sketch, "E65.2.76", {"start": v(27.09, -24.95) * mm, "mid": v(26.77, -25.09) * mm, "end": v(26.58, -25.38) * mm});
            skLineSegment(sketch, "E65.2.77", {"start": v(27.6, -24.04) * mm, "end": v(27.09, -24.95) * mm});
            skArc(sketch, "E65.2.78", {"start": v(32.23, -31.93) * mm, "mid": v(32.3, -31.42) * mm, "end": v(32.27, -30.9) * mm});
            skArc(sketch, "E65.2.79", {"start": v(26.38, -39.72) * mm, "mid": v(28, -38.7) * mm, "end": v(29.25, -37.26) * mm});
            skArc(sketch, "E65.2.80", {"start": v(29.25, -37.26) * mm, "mid": v(30.93, -34.7) * mm, "end": v(32.23, -31.93) * mm});
            skLineSegment(sketch, "E65.2.81", {"start": v(31.34, -28.48) * mm, "end": v(32.27, -30.9) * mm});
            skArc(sketch, "E65.2.82", {"start": v(30.91, -19.5) * mm, "mid": v(30.05, -20.12) * mm, "end": v(29.89, -21.16) * mm});
            skLineSegment(sketch, "E65.2.84", {"start": v(31.1, -32.14) * mm, "end": v(29.76, -34.61) * mm});
            skLineSegment(sketch, "E65.2.85", {"start": v(22.29, -35.05) * mm, "end": v(21.89, -34.72) * mm});
            skArc(sketch, "E65.2.86", {"start": v(31.1, -32.14) * mm, "mid": v(31.33, -31.46) * mm, "end": v(31.33, -30.74) * mm});
            skLineSegment(sketch, "E65.2.87", {"start": v(27.24, -34.7) * mm, "end": v(25.53, -37.95) * mm});
            skArc(sketch, "E65.2.88", {"start": v(26.5, -38.47) * mm, "mid": v(27.5, -37.87) * mm, "end": v(28.32, -37.04) * mm});
            skLineSegment(sketch, "E65.2.89", {"start": v(30.12, -29.62) * mm, "end": v(27.97, -33.44) * mm});
            skArc(sketch, "E65.2.90", {"start": v(22.55, -35.27) * mm, "mid": v(22.42, -35.16) * mm, "end": v(22.29, -35.05) * mm});
            skArc(sketch, "E65.2.91", {"start": v(25.53, -37.95) * mm, "mid": v(25.53, -38.15) * mm, "end": v(25.62, -38.33) * mm});
            skArc(sketch, "E65.2.92", {"start": v(21.8, -34.3) * mm, "mid": v(21.77, -34.53) * mm, "end": v(21.89, -34.72) * mm});
            skArc(sketch, "E65.2.93", {"start": v(25.62, -38.33) * mm, "mid": v(26.03, -38.52) * mm, "end": v(26.5, -38.47) * mm});
            skLineSegment(sketch, "E65.2.94", {"start": v(19.82, -38.59) * mm, "end": v(19.46, -39.57) * mm});
            skArc(sketch, "E65.2.95", {"start": v(21.35, -41.4) * mm, "mid": v(21.82, -41.38) * mm, "end": v(22.1, -41) * mm});
            skLineSegment(sketch, "E65.2.96", {"start": v(29.27, -35.75) * mm, "end": v(28.32, -37.04) * mm});
            skArc(sketch, "E65.2.97", {"start": v(20.46, -41.02) * mm, "mid": v(21.01, -41.04) * mm, "end": v(21.56, -41.04) * mm});
            skArc(sketch, "E65.2.98", {"start": v(21.16, -42.71) * mm, "mid": v(21.2, -42.69) * mm, "end": v(21.26, -42.66) * mm});
            skArc(sketch, "E65.2.99", {"start": v(27.77, -34.5) * mm, "mid": v(27.45, -34.45) * mm, "end": v(27.24, -34.7) * mm});
            skArc(sketch, "E65.2.100", {"start": v(29.36, -34.73) * mm, "mid": v(29.66, -34.71) * mm, "end": v(29.79, -34.44) * mm});
            skLineSegment(sketch, "E65.2.101", {"start": v(28.25, -34.17) * mm, "end": v(29.36, -34.73) * mm});
            skArc(sketch, "E65.2.102", {"start": v(27.97, -33.44) * mm, "mid": v(27.93, -33.88) * mm, "end": v(28.25, -34.17) * mm});
            skArc(sketch, "E65.2.103", {"start": v(29.27, -35.75) * mm, "mid": v(29.28, -35.46) * mm, "end": v(29.07, -35.25) * mm});
            skArc(sketch, "E65.2.104", {"start": v(29.1, -35.26) * mm, "mid": v(29.1, -35.26) * mm, "end": v(29.1, -35.26) * mm});
            skLineSegment(sketch, "E65.2.105", {"start": v(29.14, -35.28) * mm, "end": v(27.77, -34.5) * mm});
            skLineSegment(sketch, "E65.2.106", {"start": v(21.35, -41.4) * mm, "end": v(21.56, -41.04) * mm});
            skArc(sketch, "E65.2.107", {"start": v(31.85, -19.63) * mm, "mid": v(31.76, -19.17) * mm, "end": v(31.29, -19.25) * mm});
            skLineSegment(sketch, "E65.2.108", {"start": v(31.33, -30.74) * mm, "end": v(30.77, -29.63) * mm});
            skArc(sketch, "E65.2.109", {"start": v(30.78, -29.67) * mm, "mid": v(30.47, -29.43) * mm, "end": v(30.12, -29.62) * mm});
            skLineSegment(sketch, "E65.2.110", {"start": v(31.87, -19.6) * mm, "end": v(31.69, -19.92) * mm});
            skArc(sketch, "E65.2.111", {"start": v(31.11, -19.22) * mm, "mid": v(31, -19.36) * mm, "end": v(30.91, -19.5) * mm});
            skLineSegment(sketch, "E65.2.112", {"start": v(31.29, -19.25) * mm, "end": v(31.23, -19.35) * mm});
            skArc(sketch, "E65.2.113", {"start": v(31.23, -19.35) * mm, "mid": v(31.17, -19.29) * mm, "end": v(31.11, -19.22) * mm});
            skLineSegment(sketch, "E65.2.114", {"start": v(18.85, -40.9) * mm, "end": v(18.56, -40.89) * mm});
            skArc(sketch, "E65.2.115", {"start": v(30.79, -29.67) * mm, "mid": v(30.79, -29.67) * mm, "end": v(30.78, -29.67) * mm});
            skArc(sketch, "E65.2.116", {"start": v(18.75, -41.11) * mm, "mid": v(18.91, -41.57) * mm, "end": v(19.37, -41.4) * mm});
            skLineSegment(sketch, "E65.2.117", {"start": v(20.46, -41.02) * mm, "end": v(19.59, -40.96) * mm});
            skArc(sketch, "E65.2.118", {"start": v(19.46, -39.57) * mm, "mid": v(18.85, -40.12) * mm, "end": v(18.56, -40.89) * mm});
            skLineSegment(sketch, "E65.2.119", {"start": v(19.37, -41.4) * mm, "end": v(19.59, -40.96) * mm});
            skLineSegment(sketch, "E65.2.120", {"start": v(18.75, -41.11) * mm, "end": v(18.85, -40.9) * mm});
            skPoint(sketch, "E65.center", {"position": v(0, -17.7) * mm});
            skCircle(sketch, "E66", {"center": v(0, -17.7) * mm, "radius": 11 * mm});
            skPoint(sketch, "E67", {"position": v(-1.7, 9.32) * mm});
            skPoint(sketch, "E68", {"position": v(24.24, -29.74) * mm});
            skPoint(sketch, "E69", {"position": v(-22.55, -32.67) * mm});
            skLineSegment(sketch, "E70", {"start": v(-6.88, 9.15) * mm, "end": v(-5.76, 9.19) * mm});
            skPoint(sketch, "E71", {"position": v(-4.29, 9.23) * mm});
            skLineSegment(sketch, "E72", {"start": v(2.17, 9.45) * mm, "end": v(3.5, 9.5) * mm});
            skPoint(sketch, "E73", {"position": v(0.9, 9.4) * mm});
            skPoint(sketch, "E74.second.point", {"position": v(10.56, -14.63) * mm});
            skArc(sketch, "E75.0", {"start": v(-5.76, 9.19) * mm, "mid": v(-9.78, 0.92) * mm, "end": v(-8.91, -8.23) * mm});
            skArc(sketch, "E76.trimOffspring", {"start": v(2.17, 9.45) * mm, "mid": v(-4.34, 3.25) * mm, "end": v(-5.02, -5.7) * mm});
            skArc(sketch, "E77.trimOffspring", {"start": v(-8.91, -8.23) * mm, "mid": v(-12.98, -18.38) * mm, "end": v(-7.87, -28.04) * mm});
            skArc(sketch, "E78.1.0", {"start": v(-20.4, -36.13) * mm, "mid": v(-11.24, -35.47) * mm, "end": v(-3.74, -30.15) * mm});
            skArc(sketch, "E78.1.1", {"start": v(-24.6, -29.4) * mm, "mid": v(-15.97, -31.93) * mm, "end": v(-7.87, -28.04) * mm});
            skArc(sketch, "E78.2.0", {"start": v(26.16, -26.16) * mm, "mid": v(21.01, -18.54) * mm, "end": v(12.65, -14.71) * mm});
            skArc(sketch, "E78.2.1", {"start": v(22.43, -33.15) * mm, "mid": v(20.31, -24.41) * mm, "end": v(12.9, -19.34) * mm});
            skLineSegment(sketch, "E79.trimOffspring", {"start": v(-24.6, -29.4) * mm, "end": v(-25.3, -28.26) * mm});
            skArc(sketch, "E80.trimOffspring", {"start": v(-3.74, -30.15) * mm, "mid": v(7.08, -28.6) * mm, "end": v(12.9, -19.34) * mm});
            skLineSegment(sketch, "E81.trimOffspring", {"start": v(22.43, -33.15) * mm, "end": v(21.8, -34.32) * mm});
            skArc(sketch, "E82.trimOffspring", {"start": v(12.65, -14.71) * mm, "mid": v(5.9, -6.12) * mm, "end": v(-5.02, -5.7) * mm});
            skSolve(sketch);
        }
        {
            var Q0;
            {var subQ37=sQuery(id+"F0.wireOp",EDGE,"E0");Q0=makeQuery(id+"F0.imprint","IMPRINT",FACE,{"disambiguationData":[TD([[makeQuery(id+"F0.imprint","IMPRINT",EDGE,{"derivedFrom":subQ37}),1.0]])]});}
            extrude(context, id + "F1", {"entities" : qUnion([Q0]), "depth" : 7.62 * mm, "offsetDistance" : 25 * mm});
        }
        {
            var Q0;
            Q0=makeQuery(id+"F1.opExtrude","CAP_FACE",FACE,{"disambiguationData":[OSD([sQuery(id+"F0.wireOp",EDGE,"E0"),sQuery(id+"F0.wireOp",EDGE,"E1"),sQuery(id+"F0.wireOp",EDGE,"E2"),sQuery(id+"F0.wireOp",EDGE,"E3"),sQuery(id+"F0.wireOp",EDGE,"E6"),sQuery(id+"F0.wireOp",EDGE,"E7"),sQuery(id+"F0.wireOp",EDGE,"E12"),sQuery(id+"F0.wireOp",EDGE,"E13"),sQuery(id+"F0.wireOp",EDGE,"E15.trimOffspring"),sQuery(id+"F0.wireOp",EDGE,"E17.trimOffspring"),sQuery(id+"F0.wireOp",EDGE,"E19"),sQuery(id+"F0.wireOp",EDGE,"E21"),sQuery(id+"F0.wireOp",EDGE,"E22"),sQuery(id+"F0.wireOp",EDGE,"E23.trimOffspring"),sQuery(id+"F0.wireOp",EDGE,"E24"),sQuery(id+"F0.wireOp",EDGE,"E25"),sQuery(id+"F0.wireOp",EDGE,"E26"),sQuery(id+"F0.wireOp",EDGE,"E27"),sQuery(id+"F0.wireOp",EDGE,"E29"),sQuery(id+"F0.wireOp",EDGE,"E30.trimOffspring"),sQuery(id+"F0.wireOp",EDGE,"E31"),sQuery(id+"F0.wireOp",EDGE,"E32"),sQuery(id+"F0.wireOp",EDGE,"E35.trimOffspring"),sQuery(id+"F0.wireOp",EDGE,"E37"),sQuery(id+"F0.wireOp",EDGE,"E38"),sQuery(id+"F0.wireOp",EDGE,"E39.trimOffspring"),sQuery(id+"F0.wireOp",EDGE,"E41"),sQuery(id+"F0.wireOp",EDGE,"E42"),sQuery(id+"F0.wireOp",EDGE,"E43"),sQuery(id+"F0.wireOp",EDGE,"E44"),sQuery(id+"F0.wireOp",EDGE,"E45"),sQuery(id+"F0.wireOp",EDGE,"E46"),sQuery(id+"F0.wireOp",EDGE,"E47"),sQuery(id+"F0.wireOp",EDGE,"E48.trimOffspring"),sQuery(id+"F0.wireOp",EDGE,"E50"),sQuery(id+"F0.wireOp",EDGE,"E51"),sQuery(id+"F0.wireOp",EDGE,"E54"),sQuery(id+"F0.wireOp",EDGE,"E55"),sQuery(id+"F0.wireOp",EDGE,"E56"),sQuery(id+"F0.wireOp",EDGE,"E57"),sQuery(id+"F0.wireOp",EDGE,"E58.trimOffspring"),sQuery(id+"F0.wireOp",EDGE,"E59.trimOffspring"),sQuery(id+"F0.wireOp",EDGE,"E61.trimOffspring"),sQuery(id+"F0.wireOp",EDGE,"E62"),sQuery(id+"F0.wireOp",EDGE,"E63"),sQuery(id+"F0.wireOp",EDGE,"E64.trimOffspring"),sQuery(id+"F0.wireOp",EDGE,"E65.1.40"),sQuery(id+"F0.wireOp",EDGE,"E65.1.43"),sQuery(id+"F0.wireOp",EDGE,"E65.1.65"),sQuery(id+"F0.wireOp",EDGE,"E65.1.67"),sQuery(id+"F0.wireOp",EDGE,"E65.1.70"),sQuery(id+"F0.wireOp",EDGE,"E65.1.75"),sQuery(id+"F0.wireOp",EDGE,"E65.1.76"),sQuery(id+"F0.wireOp",EDGE,"E65.1.77"),sQuery(id+"F0.wireOp",EDGE,"E65.1.78"),sQuery(id+"F0.wireOp",EDGE,"E65.1.79"),sQuery(id+"F0.wireOp",EDGE,"E65.1.80"),sQuery(id+"F0.wireOp",EDGE,"E65.1.81"),sQuery(id+"F0.wireOp",EDGE,"E65.1.82"),sQuery(id+"F0.wireOp",EDGE,"E65.1.84"),sQuery(id+"F0.wireOp",EDGE,"E65.1.85"),sQuery(id+"F0.wireOp",EDGE,"E65.1.86"),sQuery(id+"F0.wireOp",EDGE,"E65.1.87"),sQuery(id+"F0.wireOp",EDGE,"E65.1.88"),sQuery(id+"F0.wireOp",EDGE,"E65.1.89"),sQuery(id+"F0.wireOp",EDGE,"E65.1.90"),sQuery(id+"F0.wireOp",EDGE,"E65.1.91"),sQuery(id+"F0.wireOp",EDGE,"E65.1.92"),sQuery(id+"F0.wireOp",EDGE,"E65.1.93"),sQuery(id+"F0.wireOp",EDGE,"E65.1.94"),sQuery(id+"F0.wireOp",EDGE,"E65.1.95"),sQuery(id+"F0.wireOp",EDGE,"E65.1.96"),sQuery(id+"F0.wireOp",EDGE,"E65.1.97"),sQuery(id+"F0.wireOp",EDGE,"E65.1.99"),sQuery(id+"F0.wireOp",EDGE,"E65.1.100"),sQuery(id+"F0.wireOp",EDGE,"E65.1.101"),sQuery(id+"F0.wireOp",EDGE,"E65.1.102"),sQuery(id+"F0.wireOp",EDGE,"E65.1.103"),sQuery(id+"F0.wireOp",EDGE,"E65.1.105"),sQuery(id+"F0.wireOp",EDGE,"E65.1.106"),sQuery(id+"F0.wireOp",EDGE,"E65.1.107"),sQuery(id+"F0.wireOp",EDGE,"E65.1.108"),sQuery(id+"F0.wireOp",EDGE,"E65.1.109"),sQuery(id+"F0.wireOp",EDGE,"E65.1.110"),sQuery(id+"F0.wireOp",EDGE,"E65.1.111"),sQuery(id+"F0.wireOp",EDGE,"E65.1.112"),sQuery(id+"F0.wireOp",EDGE,"E65.1.113"),sQuery(id+"F0.wireOp",EDGE,"E65.1.114"),sQuery(id+"F0.wireOp",EDGE,"E65.1.116"),sQuery(id+"F0.wireOp",EDGE,"E65.1.117"),sQuery(id+"F0.wireOp",EDGE,"E65.1.118"),sQuery(id+"F0.wireOp",EDGE,"E65.1.119"),sQuery(id+"F0.wireOp",EDGE,"E65.1.120"),sQuery(id+"F0.wireOp",EDGE,"E65.2.40"),sQuery(id+"F0.wireOp",EDGE,"E65.2.43"),sQuery(id+"F0.wireOp",EDGE,"E65.2.65"),sQuery(id+"F0.wireOp",EDGE,"E65.2.67"),sQuery(id+"F0.wireOp",EDGE,"E65.2.70"),sQuery(id+"F0.wireOp",EDGE,"E65.2.75"),sQuery(id+"F0.wireOp",EDGE,"E65.2.76"),sQuery(id+"F0.wireOp",EDGE,"E65.2.77"),sQuery(id+"F0.wireOp",EDGE,"E65.2.78"),sQuery(id+"F0.wireOp",EDGE,"E65.2.79"),sQuery(id+"F0.wireOp",EDGE,"E65.2.80"),sQuery(id+"F0.wireOp",EDGE,"E65.2.81"),sQuery(id+"F0.wireOp",EDGE,"E65.2.82"),sQuery(id+"F0.wireOp",EDGE,"E65.2.84"),sQuery(id+"F0.wireOp",EDGE,"E65.2.85"),sQuery(id+"F0.wireOp",EDGE,"E65.2.86"),sQuery(id+"F0.wireOp",EDGE,"E65.2.87"),sQuery(id+"F0.wireOp",EDGE,"E65.2.88"),sQuery(id+"F0.wireOp",EDGE,"E65.2.89"),sQuery(id+"F0.wireOp",EDGE,"E65.2.90"),sQuery(id+"F0.wireOp",EDGE,"E65.2.91"),sQuery(id+"F0.wireOp",EDGE,"E65.2.92"),sQuery(id+"F0.wireOp",EDGE,"E65.2.93"),sQuery(id+"F0.wireOp",EDGE,"E65.2.94"),sQuery(id+"F0.wireOp",EDGE,"E65.2.95"),sQuery(id+"F0.wireOp",EDGE,"E65.2.96"),sQuery(id+"F0.wireOp",EDGE,"E65.2.97"),sQuery(id+"F0.wireOp",EDGE,"E65.2.99"),sQuery(id+"F0.wireOp",EDGE,"E65.2.100"),sQuery(id+"F0.wireOp",EDGE,"E65.2.101"),sQuery(id+"F0.wireOp",EDGE,"E65.2.102"),sQuery(id+"F0.wireOp",EDGE,"E65.2.103"),sQuery(id+"F0.wireOp",EDGE,"E65.2.105"),sQuery(id+"F0.wireOp",EDGE,"E65.2.106"),sQuery(id+"F0.wireOp",EDGE,"E65.2.107"),sQuery(id+"F0.wireOp",EDGE,"E65.2.108"),sQuery(id+"F0.wireOp",EDGE,"E65.2.109"),sQuery(id+"F0.wireOp",EDGE,"E65.2.110"),sQuery(id+"F0.wireOp",EDGE,"E65.2.111"),sQuery(id+"F0.wireOp",EDGE,"E65.2.112"),sQuery(id+"F0.wireOp",EDGE,"E65.2.113"),sQuery(id+"F0.wireOp",EDGE,"E65.2.114"),sQuery(id+"F0.wireOp",EDGE,"E65.2.116"),sQuery(id+"F0.wireOp",EDGE,"E65.2.117"),sQuery(id+"F0.wireOp",EDGE,"E65.2.118"),sQuery(id+"F0.wireOp",EDGE,"E65.2.119"),sQuery(id+"F0.wireOp",EDGE,"E65.2.120"),sQuery(id+"F0.wireOp",EDGE,"E66"),sQuery(id+"F0.wireOp",EDGE,"E70"),sQuery(id+"F0.wireOp",EDGE,"E72"),sQuery(id+"F0.wireOp",EDGE,"E75.0"),sQuery(id+"F0.wireOp",EDGE,"E76.trimOffspring"),sQuery(id+"F0.wireOp",EDGE,"E77.trimOffspring"),sQuery(id+"F0.wireOp",EDGE,"E78.1.0"),sQuery(id+"F0.wireOp",EDGE,"E78.1.1"),sQuery(id+"F0.wireOp",EDGE,"E78.2.0"),sQuery(id+"F0.wireOp",EDGE,"E78.2.1"),sQuery(id+"F0.wireOp",EDGE,"E79.trimOffspring"),sQuery(id+"F0.wireOp",EDGE,"E80.trimOffspring"),sQuery(id+"F0.wireOp",EDGE,"E81.trimOffspring"),sQuery(id+"F0.wireOp",EDGE,"E82.trimOffspring")])],"isStart":false});
            var Q1;
            Q1=makeQuery(id+"F1.opExtrude","CAP_FACE",FACE,{"disambiguationData":[OSD([sQuery(id+"F0.wireOp",EDGE,"E0"),sQuery(id+"F0.wireOp",EDGE,"E1"),sQuery(id+"F0.wireOp",EDGE,"E2"),sQuery(id+"F0.wireOp",EDGE,"E3"),sQuery(id+"F0.wireOp",EDGE,"E6"),sQuery(id+"F0.wireOp",EDGE,"E7"),sQuery(id+"F0.wireOp",EDGE,"E12"),sQuery(id+"F0.wireOp",EDGE,"E13"),sQuery(id+"F0.wireOp",EDGE,"E15.trimOffspring"),sQuery(id+"F0.wireOp",EDGE,"E17.trimOffspring"),sQuery(id+"F0.wireOp",EDGE,"E19"),sQuery(id+"F0.wireOp",EDGE,"E21"),sQuery(id+"F0.wireOp",EDGE,"E22"),sQuery(id+"F0.wireOp",EDGE,"E23.trimOffspring"),sQuery(id+"F0.wireOp",EDGE,"E24"),sQuery(id+"F0.wireOp",EDGE,"E25"),sQuery(id+"F0.wireOp",EDGE,"E26"),sQuery(id+"F0.wireOp",EDGE,"E27"),sQuery(id+"F0.wireOp",EDGE,"E29"),sQuery(id+"F0.wireOp",EDGE,"E30.trimOffspring"),sQuery(id+"F0.wireOp",EDGE,"E31"),sQuery(id+"F0.wireOp",EDGE,"E32"),sQuery(id+"F0.wireOp",EDGE,"E35.trimOffspring"),sQuery(id+"F0.wireOp",EDGE,"E37"),sQuery(id+"F0.wireOp",EDGE,"E38"),sQuery(id+"F0.wireOp",EDGE,"E39.trimOffspring"),sQuery(id+"F0.wireOp",EDGE,"E41"),sQuery(id+"F0.wireOp",EDGE,"E42"),sQuery(id+"F0.wireOp",EDGE,"E43"),sQuery(id+"F0.wireOp",EDGE,"E44"),sQuery(id+"F0.wireOp",EDGE,"E45"),sQuery(id+"F0.wireOp",EDGE,"E46"),sQuery(id+"F0.wireOp",EDGE,"E47"),sQuery(id+"F0.wireOp",EDGE,"E48.trimOffspring"),sQuery(id+"F0.wireOp",EDGE,"E50"),sQuery(id+"F0.wireOp",EDGE,"E51"),sQuery(id+"F0.wireOp",EDGE,"E54"),sQuery(id+"F0.wireOp",EDGE,"E55"),sQuery(id+"F0.wireOp",EDGE,"E56"),sQuery(id+"F0.wireOp",EDGE,"E57"),sQuery(id+"F0.wireOp",EDGE,"E58.trimOffspring"),sQuery(id+"F0.wireOp",EDGE,"E59.trimOffspring"),sQuery(id+"F0.wireOp",EDGE,"E61.trimOffspring"),sQuery(id+"F0.wireOp",EDGE,"E62"),sQuery(id+"F0.wireOp",EDGE,"E63"),sQuery(id+"F0.wireOp",EDGE,"E64.trimOffspring"),sQuery(id+"F0.wireOp",EDGE,"E65.1.40"),sQuery(id+"F0.wireOp",EDGE,"E65.1.43"),sQuery(id+"F0.wireOp",EDGE,"E65.1.65"),sQuery(id+"F0.wireOp",EDGE,"E65.1.67"),sQuery(id+"F0.wireOp",EDGE,"E65.1.70"),sQuery(id+"F0.wireOp",EDGE,"E65.1.75"),sQuery(id+"F0.wireOp",EDGE,"E65.1.76"),sQuery(id+"F0.wireOp",EDGE,"E65.1.77"),sQuery(id+"F0.wireOp",EDGE,"E65.1.78"),sQuery(id+"F0.wireOp",EDGE,"E65.1.79"),sQuery(id+"F0.wireOp",EDGE,"E65.1.80"),sQuery(id+"F0.wireOp",EDGE,"E65.1.81"),sQuery(id+"F0.wireOp",EDGE,"E65.1.82"),sQuery(id+"F0.wireOp",EDGE,"E65.1.84"),sQuery(id+"F0.wireOp",EDGE,"E65.1.85"),sQuery(id+"F0.wireOp",EDGE,"E65.1.86"),sQuery(id+"F0.wireOp",EDGE,"E65.1.87"),sQuery(id+"F0.wireOp",EDGE,"E65.1.88"),sQuery(id+"F0.wireOp",EDGE,"E65.1.89"),sQuery(id+"F0.wireOp",EDGE,"E65.1.90"),sQuery(id+"F0.wireOp",EDGE,"E65.1.91"),sQuery(id+"F0.wireOp",EDGE,"E65.1.92"),sQuery(id+"F0.wireOp",EDGE,"E65.1.93"),sQuery(id+"F0.wireOp",EDGE,"E65.1.94"),sQuery(id+"F0.wireOp",EDGE,"E65.1.95"),sQuery(id+"F0.wireOp",EDGE,"E65.1.96"),sQuery(id+"F0.wireOp",EDGE,"E65.1.97"),sQuery(id+"F0.wireOp",EDGE,"E65.1.99"),sQuery(id+"F0.wireOp",EDGE,"E65.1.100"),sQuery(id+"F0.wireOp",EDGE,"E65.1.101"),sQuery(id+"F0.wireOp",EDGE,"E65.1.102"),sQuery(id+"F0.wireOp",EDGE,"E65.1.103"),sQuery(id+"F0.wireOp",EDGE,"E65.1.105"),sQuery(id+"F0.wireOp",EDGE,"E65.1.106"),sQuery(id+"F0.wireOp",EDGE,"E65.1.107"),sQuery(id+"F0.wireOp",EDGE,"E65.1.108"),sQuery(id+"F0.wireOp",EDGE,"E65.1.109"),sQuery(id+"F0.wireOp",EDGE,"E65.1.110"),sQuery(id+"F0.wireOp",EDGE,"E65.1.111"),sQuery(id+"F0.wireOp",EDGE,"E65.1.112"),sQuery(id+"F0.wireOp",EDGE,"E65.1.113"),sQuery(id+"F0.wireOp",EDGE,"E65.1.114"),sQuery(id+"F0.wireOp",EDGE,"E65.1.116"),sQuery(id+"F0.wireOp",EDGE,"E65.1.117"),sQuery(id+"F0.wireOp",EDGE,"E65.1.118"),sQuery(id+"F0.wireOp",EDGE,"E65.1.119"),sQuery(id+"F0.wireOp",EDGE,"E65.1.120"),sQuery(id+"F0.wireOp",EDGE,"E65.2.40"),sQuery(id+"F0.wireOp",EDGE,"E65.2.43"),sQuery(id+"F0.wireOp",EDGE,"E65.2.65"),sQuery(id+"F0.wireOp",EDGE,"E65.2.67"),sQuery(id+"F0.wireOp",EDGE,"E65.2.70"),sQuery(id+"F0.wireOp",EDGE,"E65.2.75"),sQuery(id+"F0.wireOp",EDGE,"E65.2.76"),sQuery(id+"F0.wireOp",EDGE,"E65.2.77"),sQuery(id+"F0.wireOp",EDGE,"E65.2.78"),sQuery(id+"F0.wireOp",EDGE,"E65.2.79"),sQuery(id+"F0.wireOp",EDGE,"E65.2.80"),sQuery(id+"F0.wireOp",EDGE,"E65.2.81"),sQuery(id+"F0.wireOp",EDGE,"E65.2.82"),sQuery(id+"F0.wireOp",EDGE,"E65.2.84"),sQuery(id+"F0.wireOp",EDGE,"E65.2.85"),sQuery(id+"F0.wireOp",EDGE,"E65.2.86"),sQuery(id+"F0.wireOp",EDGE,"E65.2.87"),sQuery(id+"F0.wireOp",EDGE,"E65.2.88"),sQuery(id+"F0.wireOp",EDGE,"E65.2.89"),sQuery(id+"F0.wireOp",EDGE,"E65.2.90"),sQuery(id+"F0.wireOp",EDGE,"E65.2.91"),sQuery(id+"F0.wireOp",EDGE,"E65.2.92"),sQuery(id+"F0.wireOp",EDGE,"E65.2.93"),sQuery(id+"F0.wireOp",EDGE,"E65.2.94"),sQuery(id+"F0.wireOp",EDGE,"E65.2.95"),sQuery(id+"F0.wireOp",EDGE,"E65.2.96"),sQuery(id+"F0.wireOp",EDGE,"E65.2.97"),sQuery(id+"F0.wireOp",EDGE,"E65.2.99"),sQuery(id+"F0.wireOp",EDGE,"E65.2.100"),sQuery(id+"F0.wireOp",EDGE,"E65.2.101"),sQuery(id+"F0.wireOp",EDGE,"E65.2.102"),sQuery(id+"F0.wireOp",EDGE,"E65.2.103"),sQuery(id+"F0.wireOp",EDGE,"E65.2.105"),sQuery(id+"F0.wireOp",EDGE,"E65.2.106"),sQuery(id+"F0.wireOp",EDGE,"E65.2.107"),sQuery(id+"F0.wireOp",EDGE,"E65.2.108"),sQuery(id+"F0.wireOp",EDGE,"E65.2.109"),sQuery(id+"F0.wireOp",EDGE,"E65.2.110"),sQuery(id+"F0.wireOp",EDGE,"E65.2.111"),sQuery(id+"F0.wireOp",EDGE,"E65.2.112"),sQuery(id+"F0.wireOp",EDGE,"E65.2.113"),sQuery(id+"F0.wireOp",EDGE,"E65.2.114"),sQuery(id+"F0.wireOp",EDGE,"E65.2.116"),sQuery(id+"F0.wireOp",EDGE,"E65.2.117"),sQuery(id+"F0.wireOp",EDGE,"E65.2.118"),sQuery(id+"F0.wireOp",EDGE,"E65.2.119"),sQuery(id+"F0.wireOp",EDGE,"E65.2.120"),sQuery(id+"F0.wireOp",EDGE,"E66"),sQuery(id+"F0.wireOp",EDGE,"E70"),sQuery(id+"F0.wireOp",EDGE,"E72"),sQuery(id+"F0.wireOp",EDGE,"E75.0"),sQuery(id+"F0.wireOp",EDGE,"E76.trimOffspring"),sQuery(id+"F0.wireOp",EDGE,"E77.trimOffspring"),sQuery(id+"F0.wireOp",EDGE,"E78.1.0"),sQuery(id+"F0.wireOp",EDGE,"E78.1.1"),sQuery(id+"F0.wireOp",EDGE,"E78.2.0"),sQuery(id+"F0.wireOp",EDGE,"E78.2.1"),sQuery(id+"F0.wireOp",EDGE,"E79.trimOffspring"),sQuery(id+"F0.wireOp",EDGE,"E80.trimOffspring"),sQuery(id+"F0.wireOp",EDGE,"E81.trimOffspring"),sQuery(id+"F0.wireOp",EDGE,"E82.trimOffspring")])],"isStart":true});
            fillet(context, id + "F2", {"entities" : qUnion([Q0, Q1]), "radius" : .1 * mm, "tangentPropagation" : true, "allowEdgeOverflow" : false});
        }
    });
